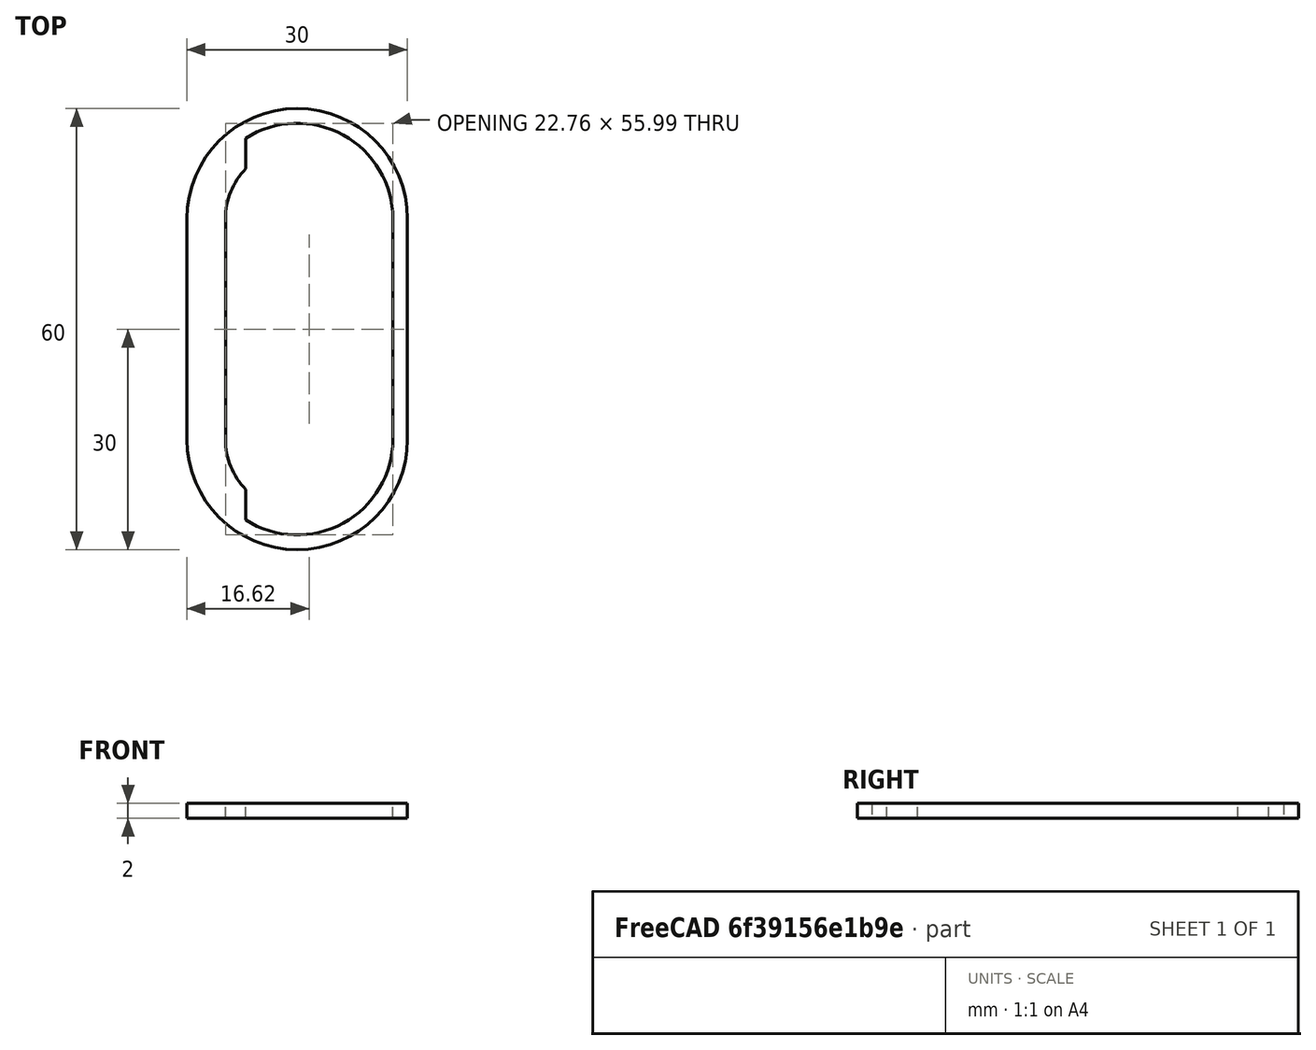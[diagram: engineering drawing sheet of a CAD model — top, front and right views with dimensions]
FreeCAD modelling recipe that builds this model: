
FCSTD DOCUMENT
Label: RecircBallRetainer
objects: Sketcher::SketchObject×1, PartDesign::Pad×1
note: 3 computed .brp shape members not serialized (recipe doc carries the construction recipe); baked Part::Feature solids carry a one-line shape summary decoded from their .brp

FEATURE [Sketcher::SketchObject] Sketch
  sketch-geometry (21):
    g0: ArcOfCircle CenterX=0 CenterY=0 CenterZ=0 NormalX=0 NormalY=0 NormalZ=1 Radius=13 StartAngle=4.14378 EndAngle=6.28319
    g1: ArcOfCircle CenterX=0 CenterY=0 CenterZ=0 NormalX=0 NormalY=0 NormalZ=1 Radius=15 StartAngle=3.14159 EndAngle=6.28319
    g2: ArcOfCircle CenterX=0 CenterY=30 CenterZ=0 NormalX=0 NormalY=0 NormalZ=1 Radius=13 StartAngle=0 EndAngle=2.13941
    g3: ArcOfCircle CenterX=0 CenterY=30 CenterZ=0 NormalX=0 NormalY=0 NormalZ=1 Radius=15 StartAngle=0 EndAngle=3.14159
    g4: LineSegment StartX=13 StartY=30 StartZ=0 EndX=13 EndY=0 EndZ=0
    g5: LineSegment [constr] StartX=13 StartY=0 StartZ=0 EndX=15 EndY=0 EndZ=0
    g6: LineSegment StartX=15 StartY=0 StartZ=0 EndX=15 EndY=30 EndZ=0
    g7: LineSegment [constr] StartX=15 StartY=30 StartZ=0 EndX=13 EndY=30 EndZ=0
    g8: LineSegment [constr] StartX=0 StartY=30 StartZ=0 EndX=13 EndY=30 EndZ=0
    g9: LineSegment [constr] StartX=13 StartY=0 StartZ=0 EndX=0 EndY=0 EndZ=0
    g10: ArcOfCircle CenterX=0 CenterY=0 CenterZ=0 NormalX=0 NormalY=0 NormalZ=1 Radius=9.76 StartAngle=3.14159 EndAngle=3.91259
    g11: LineSegment StartX=-7 StartY=-10.9545 StartZ=0 EndX=-7 EndY=-6.80129 EndZ=0
    g12: LineSegment [constr] StartX=-9.76 StartY=0 StartZ=0 EndX=0 EndY=0 EndZ=0
    g13: ArcOfCircle CenterX=0 CenterY=30 CenterZ=0 NormalX=0 NormalY=0 NormalZ=1 Radius=9.76 StartAngle=2.37059 EndAngle=3.14159
    g14: LineSegment StartX=-7 StartY=40.9545 StartZ=0 EndX=-7 EndY=36.8013 EndZ=0
    g15: LineSegment [constr] StartX=-9.76 StartY=30 StartZ=0 EndX=0 EndY=30 EndZ=0
    g16: LineSegment StartX=-15 StartY=30 StartZ=0 EndX=-15 EndY=0 EndZ=0
    g17: LineSegment StartX=-9.76 StartY=30 StartZ=0 EndX=-9.76 EndY=0 EndZ=0
    g18: LineSegment [constr] StartX=-9.76 StartY=30 StartZ=0 EndX=-15 EndY=30 EndZ=0
    g19: LineSegment [constr] StartX=-15 StartY=0 StartZ=0 EndX=-9.76 EndY=0 EndZ=0
    g20: LineSegment [constr] StartX=-7 StartY=36.8013 StartZ=0 EndX=-7 EndY=-6.80129 EndZ=0
  constraints (56):
    c: Coincident(g1,g0)
    c: Coincident(g3,g2)
    c: Coincident(g4,g2)
    c: Coincident(g4,g0)
    c: Vertical(g4)
    c: Coincident(g4,g5)
    c: Coincident(g5,g1)
    c: Horizontal(g5)
    c: Coincident(g5,g6)
    c: Coincident(g6,g3)
    c: Vertical(g6)
    c: Coincident(g6,g7)
    c: Coincident(g7,g2)
    c: Horizontal(g7)
    c: Coincident(g8,g2)
    c: Coincident(g8,g2)
    c: Horizontal(g8)
    c: Coincident(g9,g0)
    c: Coincident(g9,g0)
    c: Horizontal(g9)
    c: Coincident(g10,g0)
    c: Coincident(g11,g0)
    c: Coincident(g11,g10)
    c: Coincident(g12,g10)
    c: Coincident(g12,g0)
    c: Horizontal(g12)
    c: Coincident(g13,g2)
    c: Coincident(g14,g2)
    c: Coincident(g14,g13)
    c: Coincident(g15,g13)
    c: Coincident(g15,g2)
    c: Horizontal(g15)
    c: Coincident(g16,g3)
    c: Coincident(g16,g1)
    c: Vertical(g16)
    c: DistanceX(g7) = -2
    c: Radius(g3) = 15
    c: Coincident(g17,g13)
    c: Coincident(g17,g10)
    c: Vertical(g17)
    c: Coincident(g18,g13)
    c: Coincident(g18,g3)
    c: Horizontal(g18)
    c: Coincident(g19,g1)
    c: Coincident(g19,g10)
    c: Horizontal(g19)
    c: Vertical(g14)
    c: Vertical(g11)
    c: Coincident(g20,g13)
    c: Coincident(g20,g10)
    c: Vertical(g20)
    c: DistanceX(g2,g13) = -7
    c: Radius(g13) = 9.76
    c: DistanceY(g0,g2) = 30
    c: DistanceX(g0) = 0
    c: DistanceY(g0) = 0
FEATURE [PartDesign::Pad] Pad
  Length = 2
  MirroredExtent = false
  Sketch = -> Sketch
